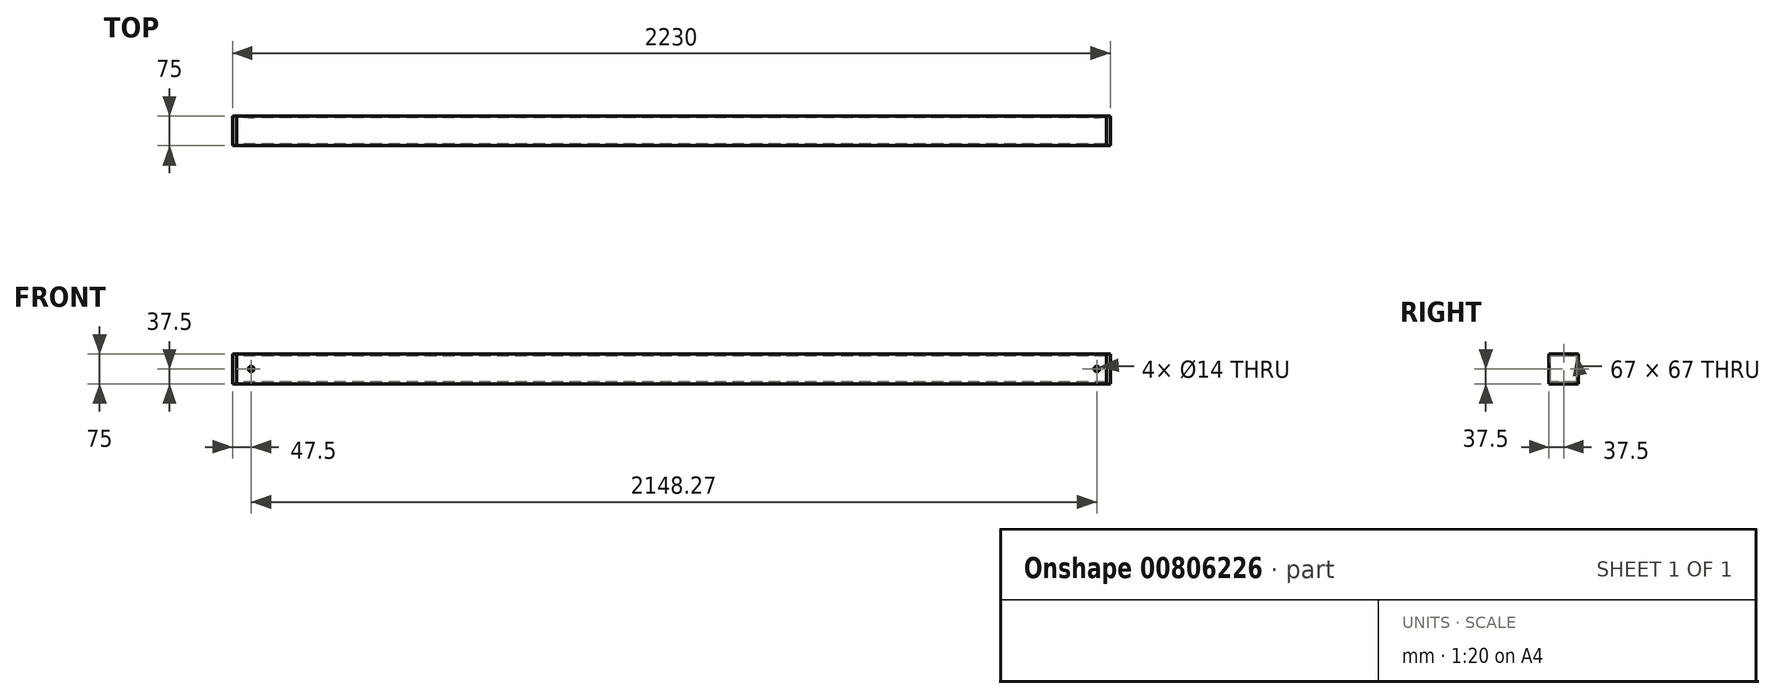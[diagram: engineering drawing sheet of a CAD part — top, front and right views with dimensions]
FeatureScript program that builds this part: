
annotation { "Feature Type Name" : "Feature", "Feature Type Description" : "" }
export const myFeature = defineFeature(function(context is Context, id is Id, definition is map)
    precondition{}
    {
        {
            var Q0;
            Q0=qCreatedBy(makeId("Right.planeOp"),FACE);
            var sketch = newSketch(context, id + "F0", { "sketchPlane" : qUnion([Q0])});
            skLineSegment(sketch, "E0.bottom", {"start": v(37.5, -37.5) * mm, "end": v(-37.5, -37.5) * mm});
            skLineSegment(sketch, "E0.top", {"start": v(37.5, 37.5) * mm, "end": v(-37.5, 37.5) * mm});
            skLineSegment(sketch, "E0.left", {"start": v(37.5, -37.5) * mm, "end": v(37.5, 37.5) * mm});
            skLineSegment(sketch, "E0.right", {"start": v(-37.5, -37.5) * mm, "end": v(-37.5, 37.5) * mm});
            skPoint(sketch, "E0.middle", {"position": v(0, 0) * mm});
            skLineSegment(sketch, "E1.0", {"start": v(-33.5, -33.5) * mm, "end": v(-33.5, 33.5) * mm});
            skLineSegment(sketch, "E1.1", {"start": v(33.5, -33.5) * mm, "end": v(-33.5, -33.5) * mm});
            skLineSegment(sketch, "E1.2", {"start": v(33.5, -33.5) * mm, "end": v(33.5, 33.5) * mm});
            skLineSegment(sketch, "E1.3", {"start": v(33.5, 33.5) * mm, "end": v(-33.5, 33.5) * mm});
            skSolve(sketch);
        }
        {
            var Q0;
            Q0=qSketchRegion(id+"F0",true);
            extrude(context, id + "F1", {"entities" : qUnion([Q0]), "depth" : 2210 * mm, "offsetDistance" : 25 * mm});
        }
        {
            var Q0;
            Q0=makeQuery(id+"F1.opExtrude","CAP_FACE",FACE,{"disambiguationData":[OSD([sQuery(id+"F0.wireOp",EDGE,"E0.bottom"),sQuery(id+"F0.wireOp",EDGE,"E0.top"),sQuery(id+"F0.wireOp",EDGE,"E0.left"),sQuery(id+"F0.wireOp",EDGE,"E0.right"),sQuery(id+"F0.wireOp",EDGE,"E1.0"),sQuery(id+"F0.wireOp",EDGE,"E1.1"),sQuery(id+"F0.wireOp",EDGE,"E1.2"),sQuery(id+"F0.wireOp",EDGE,"E1.3")])],"isStart":false});
            var sketch = newSketch(context, id + "F2", { "sketchPlane" : qUnion([Q0])});
            skLineSegment(sketch, "E2.bottom", {"start": v(37.5, -37.5) * mm, "end": v(-37.5, -37.5) * mm});
            skLineSegment(sketch, "E2.top", {"start": v(37.5, 37.5) * mm, "end": v(-37.5, 37.5) * mm});
            skLineSegment(sketch, "E2.left", {"start": v(37.5, -37.5) * mm, "end": v(37.5, 37.5) * mm});
            skLineSegment(sketch, "E2.right", {"start": v(-37.5, -37.5) * mm, "end": v(-37.5, 37.5) * mm});
            skPoint(sketch, "E2.middle", {"position": v(0, 0) * mm});
            skLineSegment(sketch, "E3.bottom", {"start": v(-37.5, 37.5) * mm, "end": v(37.5, 37.5) * mm});
            skLineSegment(sketch, "E3.top", {"start": v(-37.5, -37.5) * mm, "end": v(37.5, -37.5) * mm});
            skLineSegment(sketch, "E3.left", {"start": v(-37.5, 37.5) * mm, "end": v(-37.5, -37.5) * mm});
            skLineSegment(sketch, "E3.right", {"start": v(37.5, 37.5) * mm, "end": v(37.5, -37.5) * mm});
            skSolve(sketch);
        }
        {
            var Q0;
            Q0=qSketchRegion(id+"F2",true);
            extrude(context, id + "F3", {"entities" : qUnion([Q0]), "depth" : 10 * mm, "offsetDistance" : 25 * mm});
        }
        {
            var Q0;
            Q0=makeQuery(id+"F1.opExtrude","CAP_FACE",FACE,{"disambiguationData":[OSD([sQuery(id+"F0.wireOp",EDGE,"E0.bottom"),sQuery(id+"F0.wireOp",EDGE,"E0.top"),sQuery(id+"F0.wireOp",EDGE,"E0.left"),sQuery(id+"F0.wireOp",EDGE,"E0.right"),sQuery(id+"F0.wireOp",EDGE,"E1.0"),sQuery(id+"F0.wireOp",EDGE,"E1.1"),sQuery(id+"F0.wireOp",EDGE,"E1.2"),sQuery(id+"F0.wireOp",EDGE,"E1.3")])],"isStart":true});
            var sketch = newSketch(context, id + "F4", { "sketchPlane" : qUnion([Q0])});
            skLineSegment(sketch, "E4.bottom", {"start": v(-37.5, -37.5) * mm, "end": v(37.5, -37.5) * mm});
            skLineSegment(sketch, "E4.top", {"start": v(-37.5, 37.5) * mm, "end": v(37.5, 37.5) * mm});
            skLineSegment(sketch, "E4.left", {"start": v(-37.5, -37.5) * mm, "end": v(-37.5, 37.5) * mm});
            skLineSegment(sketch, "E4.right", {"start": v(37.5, -37.5) * mm, "end": v(37.5, 37.5) * mm});
            skSolve(sketch);
        }
        {
            var Q0;
            Q0=qSketchRegion(id+"F4",true);
            extrude(context, id + "F5", {"entities" : qUnion([Q0]), "depth" : 10 * mm, "offsetDistance" : 25 * mm});
        }
        {
            var Q0;
            Q0=makeQuery(id+"F5.opExtrude","SWEPT_FACE",FACE,{"disambiguationData":[OSD([sQuery(id+"F4.wireOp",EDGE,"E4.right")])]});
            var sketch = newSketch(context, id + "F6", { "sketchPlane" : qUnion([Q0])});
            skLineSegment(sketch, "E5", {"start": v(-10, 0) * mm, "end": v(37.5, 0) * mm});
            skCircle(sketch, "E6", {"center": v(37.5, 0) * mm, "radius": 7 * mm});
            skLineSegment(sketch, "E7", {"start": v(2233.27, 0) * mm, "end": v(2185.77, 0) * mm});
            skCircle(sketch, "E8", {"center": v(2185.77, 0) * mm, "radius": 7 * mm});
            skSolve(sketch);
        }
        {
            var Q0;
            Q0=makeQuery(id+"F6.imprint","IMPRINT",FACE,{"disambiguationData":[TD([[makeQuery(id+"F6.imprint","IMPRINT",EDGE,{"derivedFrom":sQuery(id+"F6.wireOp",EDGE,"E6")}),1.0]])]});
            var Q1;
            Q1=makeQuery(id+"F6.imprint","IMPRINT",FACE,{"disambiguationData":[TD([[makeQuery(id+"F6.imprint","IMPRINT",EDGE,{"derivedFrom":sQuery(id+"F6.wireOp",EDGE,"E8")}),1.0]])]});
            extrude(context, id + "F7", {"entities" : qUnion([Q0, Q1]), "operationType" : NewBodyOperationType.REMOVE, "oppositeDirection" : true, "depth" : 75 * mm, "offsetDistance" : 25 * mm});
        }
    });
